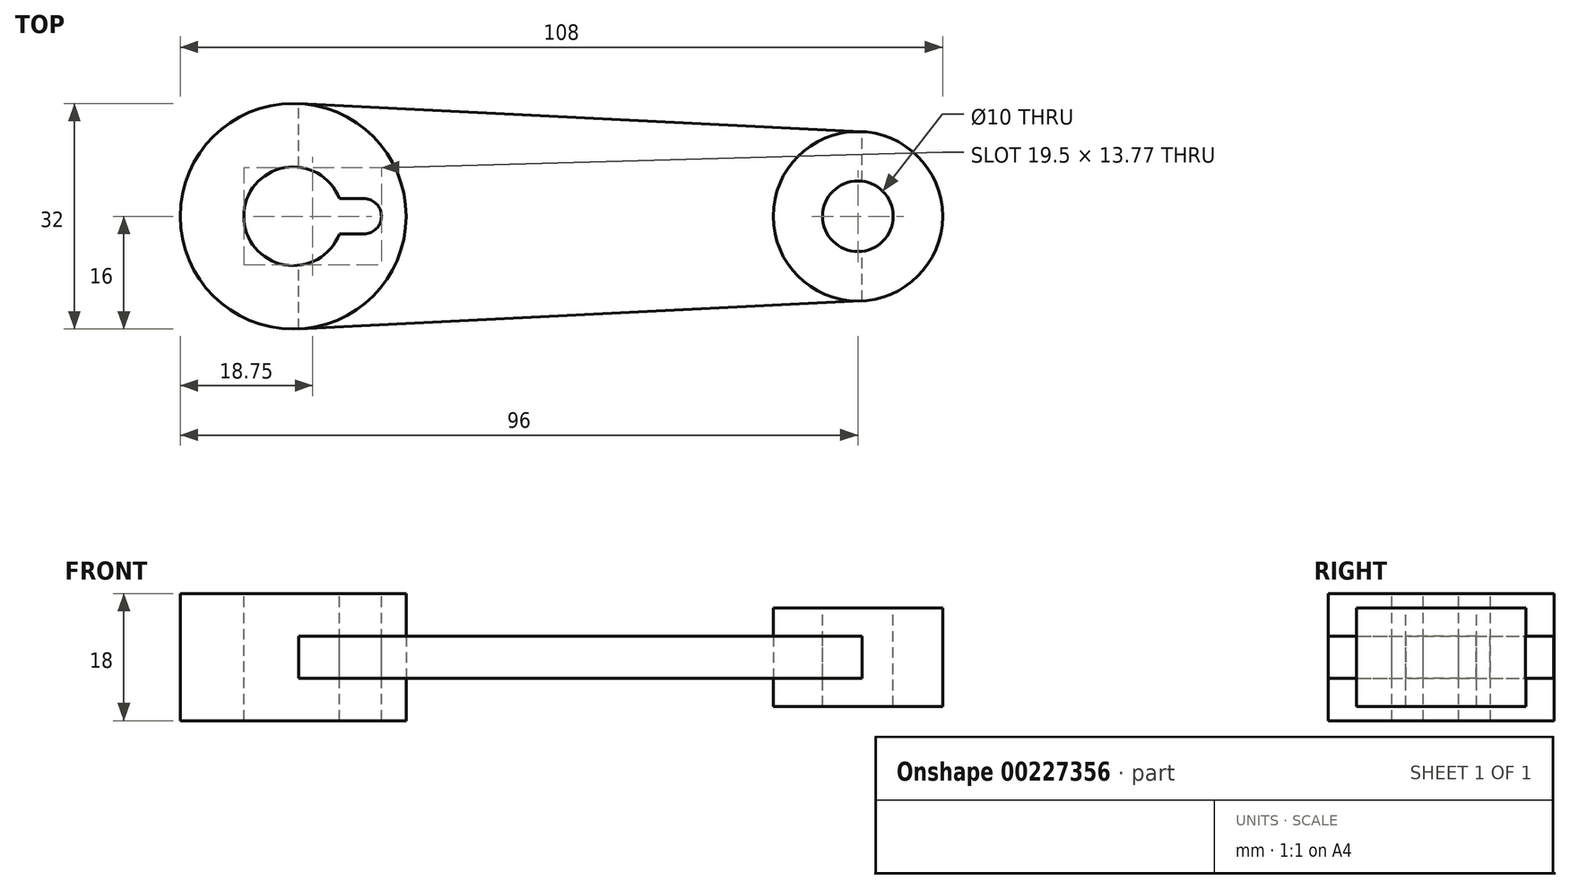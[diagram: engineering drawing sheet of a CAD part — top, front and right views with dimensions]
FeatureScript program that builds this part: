
annotation { "Feature Type Name" : "Feature", "Feature Type Description" : "" }
export const myFeature = defineFeature(function(context is Context, id is Id, definition is map)
    precondition{}
    {
        {
            var Q0;
            Q0=qCreatedBy(makeId("Top.planeOp"),FACE);
            var sketch = newSketch(context, id + "F0", { "sketchPlane" : qUnion([Q0])});
            skCircle(sketch, "E0", {"center": v(0, 0) * mm, "radius": 16 * mm});
            skSolve(sketch);
        }
        {
            var Q0;
            Q0 = qSketchRegion(id + "F0", true);
            extrude(context, id + "F1", {"entities" : qUnion([Q0]), "depth" : 9 * mm, "hasSecondDirection" : true, "secondDirectionOppositeDirection" : true, "secondDirectionDepth" : 9 * mm});
        }
        {
            var Q0;
            Q0=qCreatedBy(makeId("Top.planeOp"),FACE);
            var sketch = newSketch(context, id + "F2", { "sketchPlane" : qUnion([Q0])});
            skCircle(sketch, "E1", {"center": v(80, 0) * mm, "radius": 12 * mm});
            skSolve(sketch);
        }
        {
            var Q0;
            Q0 = qSketchRegion(id + "F2", true);
            extrude(context, id + "F3", {"entities" : qUnion([Q0]), "depth" : 7 * mm, "hasSecondDirection" : true, "secondDirectionOppositeDirection" : true, "secondDirectionDepth" : 7 * mm});
        }
        {
            var Q0;
            Q0=qCreatedBy(makeId("Top.planeOp"),FACE);
            var sketch = newSketch(context, id + "F4", { "sketchPlane" : qUnion([Q0])});
            skCircle(sketch, "E2", {"center": v(0, 0) * mm, "radius": 16 * mm, "construction": true});
            skCircle(sketch, "E3", {"center": v(80, 0) * mm, "radius": 12 * mm, "construction": true});
            skLineSegment(sketch, "E4", {"start": v(0.8, 15.98) * mm, "end": v(80.6, 11.98) * mm});
            skLineSegment(sketch, "E5", {"start": v(0.8, -15.98) * mm, "end": v(80.6, -11.98) * mm});
            skLineSegment(sketch, "E6", {"start": v(0.8, -15.98) * mm, "end": v(0.8, 15.98) * mm});
            skLineSegment(sketch, "E7", {"start": v(80.6, -11.98) * mm, "end": v(80.6, 11.98) * mm});
            skSolve(sketch);
        }
        {
            var Q0;
            Q0 = qSketchRegion(id + "F4", true);
            extrude(context, id + "F5", {"entities" : qUnion([Q0]), "depth" : 3 * mm, "hasSecondDirection" : true, "secondDirectionOppositeDirection" : true, "secondDirectionDepth" : 3 * mm});
        }
        {
            var Q0;
            Q0=makeQuery(id+"F1.opExtrude","CAP_FACE",FACE,{"disambiguationData":[OSD([sQuery(id+"F0.wireOp",EDGE,"E0")])],"isStart":false});
            var sketch = newSketch(context, id + "F6", { "sketchPlane" : qUnion([Q0])});
            skArc(sketch, "E8", {"start": v(6.54, 2.5) * mm, "mid": v(-7, 0) * mm, "end": v(6.54, -2.5) * mm});
            skLineSegment(sketch, "E9", {"start": v(6.54, 2.5) * mm, "end": v(10, 2.5) * mm});
            skLineSegment(sketch, "E10", {"start": v(12.5, 2.5) * mm, "end": v(12.5, -2.5) * mm, "construction": true});
            skLineSegment(sketch, "E11.MirrorCS", {"start": v(6.54, -2.5) * mm, "end": v(10, -2.5) * mm});
            skPoint(sketch, "E12.orphan", {"position": v(2, -2.5) * mm});
            skPoint(sketch, "E13.orphan", {"position": v(2, 2.5) * mm});
            skPoint(sketch, "E14.orphan", {"position": v(13.8, -2.5) * mm});
            skPoint(sketch, "E15.orphan", {"position": v(13.8, 2.5) * mm});
            skArc(sketch, "E16", {"start": v(10, -2.5) * mm, "mid": v(12.5, 0) * mm, "end": v(10, 2.5) * mm});
            skSolve(sketch);
        }
        {
            var Q0;
            Q0 = qSketchRegion(id + "F6", true);
            extrude(context, id + "F7", {"entities" : qUnion([Q0]), "operationType" : NewBodyOperationType.REMOVE, "endBound" : BoundingType.THROUGH_ALL, "oppositeDirection" : true, "depth" : 25 * mm});
        }
        {
            var Q0;
            Q0=makeQuery(id+"F3.opExtrude","CAP_FACE",FACE,{"disambiguationData":[OSD([sQuery(id+"F2.wireOp",EDGE,"E1")])],"isStart":false});
            var sketch = newSketch(context, id + "F8", { "sketchPlane" : qUnion([Q0])});
            skCircle(sketch, "E17", {"center": v(80, 0) * mm, "radius": 5 * mm});
            skSolve(sketch);
        }
        {
            var Q0;
            Q0 = qSketchRegion(id + "F8", true);
            extrude(context, id + "F9", {"entities" : qUnion([Q0]), "operationType" : NewBodyOperationType.REMOVE, "endBound" : BoundingType.THROUGH_ALL, "oppositeDirection" : true, "depth" : 25 * mm});
        }
    });
